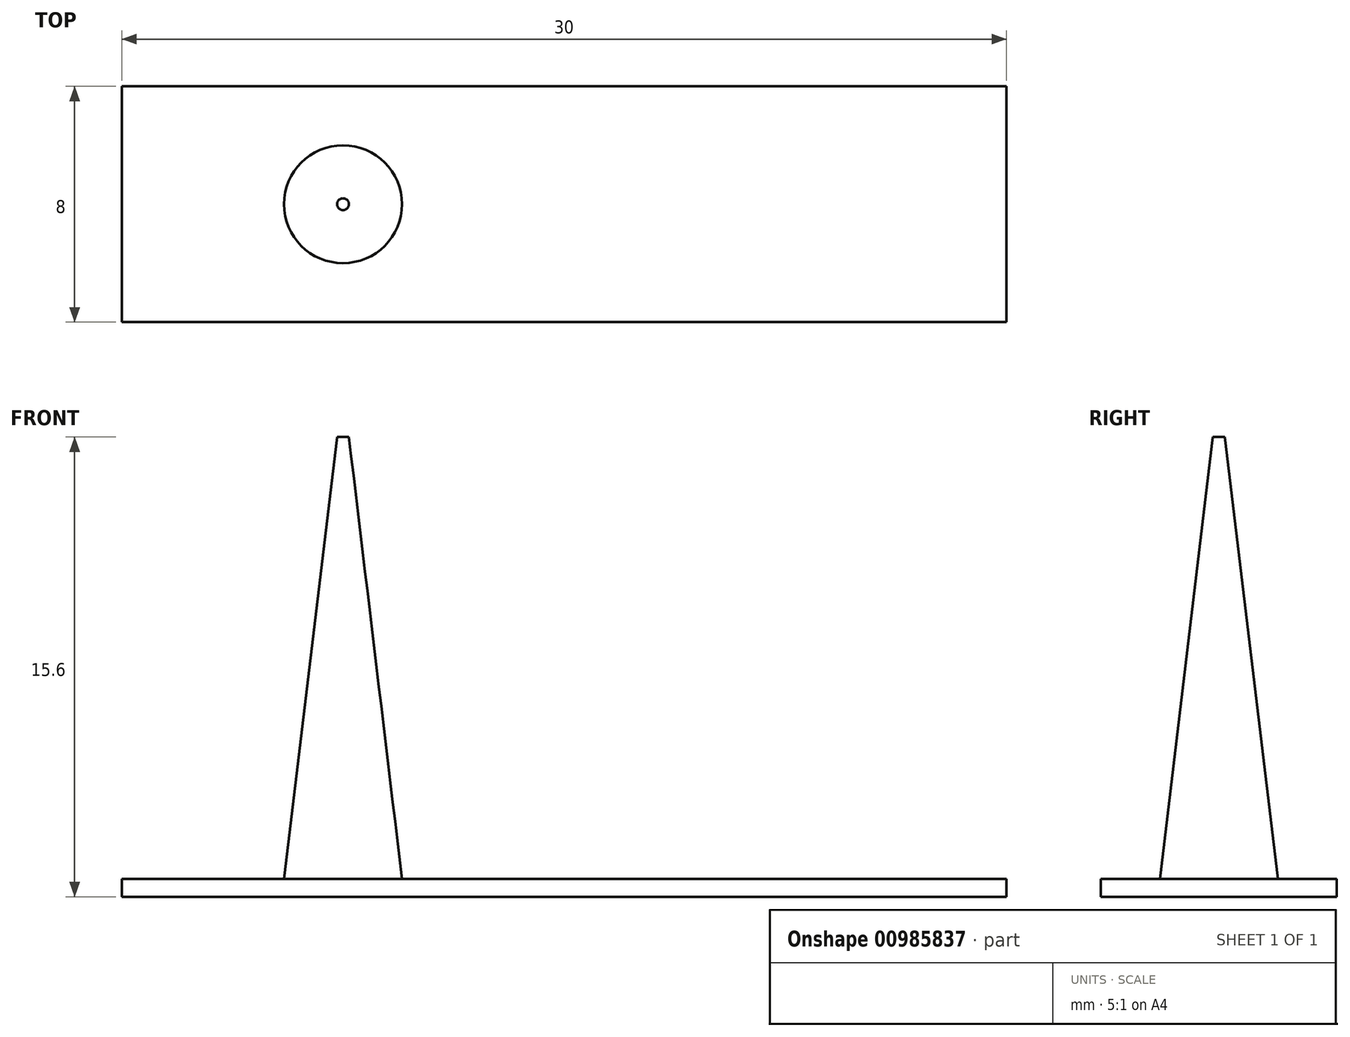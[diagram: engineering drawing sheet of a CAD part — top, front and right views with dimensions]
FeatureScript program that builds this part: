
annotation { "Feature Type Name" : "Feature", "Feature Type Description" : "" }
export const myFeature = defineFeature(function(context is Context, id is Id, definition is map)
    precondition{}
    {
        {
            var Q0;
            Q0=qCreatedBy(makeId("Top.planeOp"),FACE);
            var sketch = newSketch(context, id + "F0", { "sketchPlane" : qUnion([Q0])});
            skLineSegment(sketch, "E0.bottom", {"start": v(15, -4) * mm, "end": v(-15, -4) * mm});
            skLineSegment(sketch, "E0.top", {"start": v(15, 4) * mm, "end": v(-15, 4) * mm});
            skLineSegment(sketch, "E0.left", {"start": v(15, -4) * mm, "end": v(15, 4) * mm});
            skLineSegment(sketch, "E0.right", {"start": v(-15, -4) * mm, "end": v(-15, 4) * mm});
            skPoint(sketch, "E0.middle", {"position": v(0, 0) * mm});
            skSolve(sketch);
        }
        {
            var Q0;
            Q0=makeQuery(id+"F0.imprint","IMPRINT",FACE,{"disambiguationData":[TD([[makeQuery(id+"F0.imprint","IMPRINT",EDGE,{"derivedFrom":sQuery(id+"F0.wireOp",EDGE,"E0.bottom")}),-1.0]])]});
            extrude(context, id + "F1", {"entities" : qUnion([Q0]), "depth" : 0.6 * mm, "offsetDistance" : 25 * mm});
        }
        {
            var Q0;
            Q0=qCreatedBy(makeId("Front.planeOp"),FACE);
            var sketch = newSketch(context, id + "F2", { "sketchPlane" : qUnion([Q0])});
            skLineSegment(sketch, "E1", {"start": v(0, 15.6) * mm, "end": v(-15, 15.6) * mm});
            skPoint(sketch, "E2.0", {"position": v(-15, 0.6) * mm});
            skLineSegment(sketch, "E3", {"start": v(-7.5, 15.6) * mm, "end": v(-7.5, 0.6) * mm, "construction": true});
            skLineSegment(sketch, "E4.0", {"start": v(15, 0.6) * mm, "end": v(-15, 0.6) * mm, "construction": true});
            skLineSegment(sketch, "E5", {"start": v(-7.5, 0.6) * mm, "end": v(-5.5, 0.6) * mm});
            skLineSegment(sketch, "E6", {"start": v(-5.5, 0.6) * mm, "end": v(-7.3, 15.6) * mm});
            skLineSegment(sketch, "E7", {"start": v(-7.3, 15.6) * mm, "end": v(-7.5, 15.6) * mm});
            skLineSegment(sketch, "E8", {"start": v(-7.5, 15.6) * mm, "end": v(-7.5, 0.6) * mm});
            skSolve(sketch);
        }
        {
            var Q0;
            Q0=makeQuery(id+"F2.imprint","IMPRINT",FACE,{"disambiguationData":[TD([[makeQuery(id+"F2.imprint","IMPRINT",EDGE,{"derivedFrom":sQuery(id+"F2.wireOp",EDGE,"E5")}),1.0]])]});
            var Q1;
            Q1=sQuery(id+"F2.wireOp",EDGE,"E8");
            revolve(context, id + "F3", {"operationType" : NewBodyOperationType.ADD, "surfaceOperationType" : NewSurfaceOperationType.NEW, "entities" : qUnion([Q0]), "axis" : qUnion([Q1]), "revolveType" : RevolveType.FULL});
        }
    });
